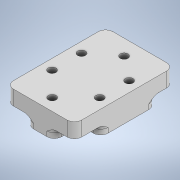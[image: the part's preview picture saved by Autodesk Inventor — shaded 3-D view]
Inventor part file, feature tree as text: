
AUTODESK INVENTOR PART (.ipt)
format: ipt  version: 2021 (Build 250183000, 183)  size: 302,080 bytes
history: native  units: mm
features: extrude x3, fillet x3, sketch x3, projected_geometry x1
ambient origin geometry x8: Origin, YZ Plane, XZ Plane, XY Plane, X Axis, Y Axis, Z Axis, Center Point
bodies: Solid1 (feature_tree)
feature tree (10):
  extrude  "Extrusion1"  Depth=3.5mm
  extrude  "Extrusion2"  Depth=10.0mm TaperAngle=0.0deg
  extrude  "Extrusion3"  Depth=3.0mm
  fillet  "Fillet2"  Radius=3.2mm
  fillet  "Fillet3"  Radius=3.2mm
  fillet  "Fillet4"  Radius=3.2mm
  sketch  "Sketch1"  dims[d1=7.0mm d2=7.0mm d3=4.2mm d4=4.2mm d5=3.5mm d6=3.5mm d7=12.15mm d10=3.5mm]
  sketch  "Sketch2"  dims[d11=15.0mm d12=10.0mm d13=0.0mm]
  sketch  "Sketch3"  dims[d15=7.5mm d16=7.5mm d17=4.2mm d18=4.2mm d19=4.2mm d20=4.2mm d21=12.15mm d24=3.5mm d25=15.0mm d26=3.2mm d27=3.2mm d28=3.2mm d29=3.2mm d30=3.2mm d31=3.2mm d32=0.0mm d33=0.0mm d41=12.0mm d44=3.5mm d45=15.0mm d46=7.4mm d47=7.4mm d48=7.4mm d49=7.4mm d50=7.4mm d52=4.0mm d53=0.0mm d55=3.0mm d56=2.0mm d57=3.0mm d58=22.0mm d59=13.0mm d60=13.0mm d61=17.15mm d62=12.0mm d63=12.0mm d64=17.15mm d65=0.872665mm d66=0.872665mm d67=0.5mm d68=0.872665mm]
  projected_geometry  "Projected Loop1"
